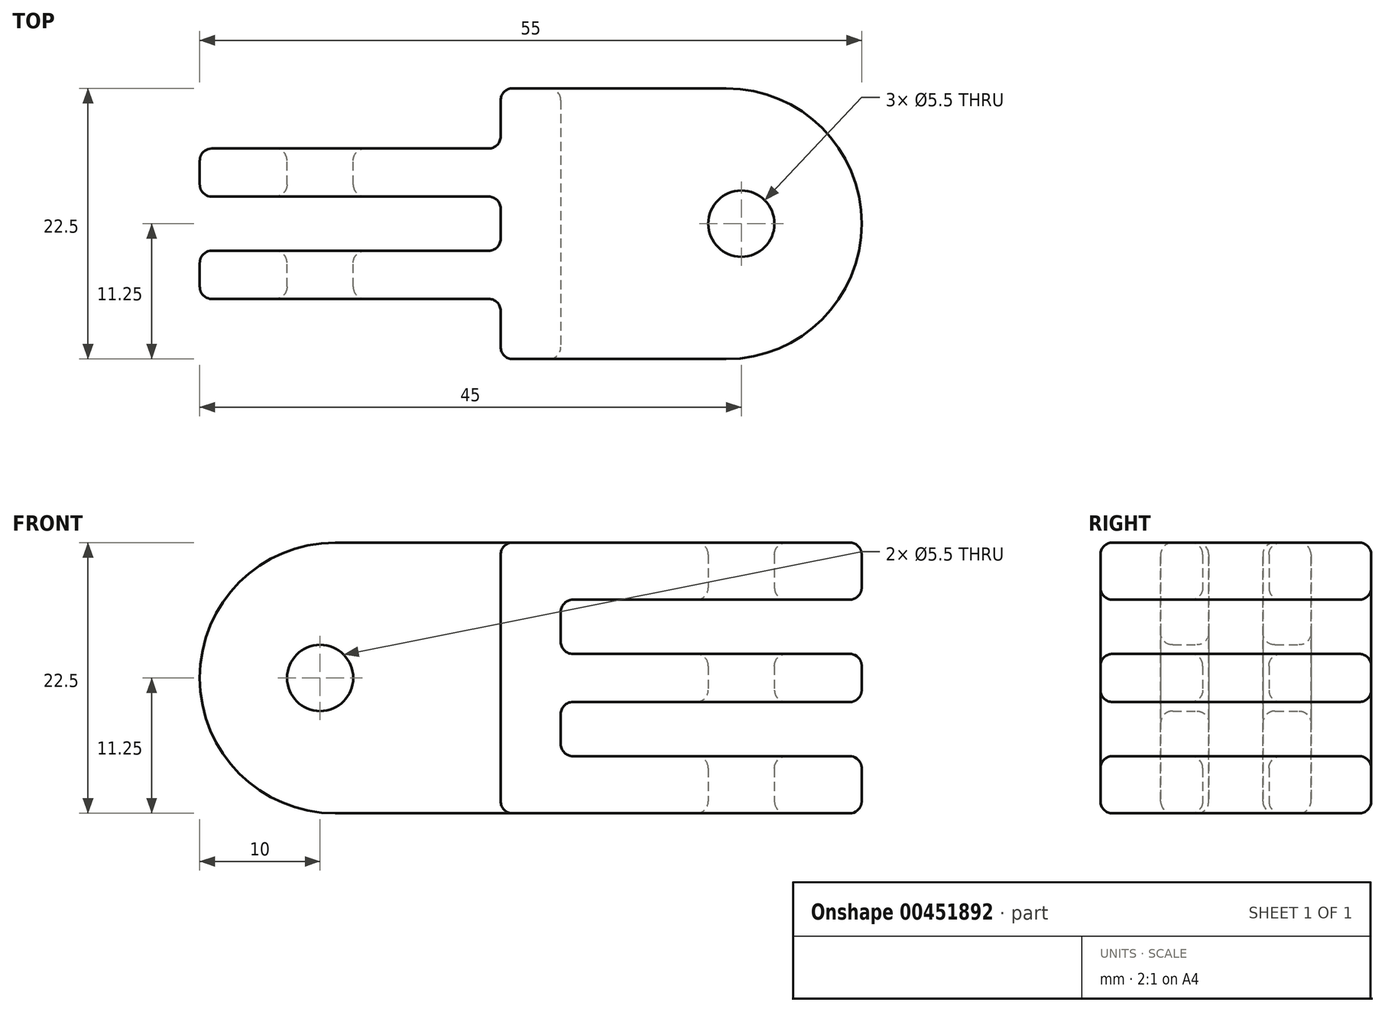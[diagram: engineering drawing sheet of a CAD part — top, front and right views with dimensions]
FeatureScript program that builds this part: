
annotation { "Feature Type Name" : "Feature", "Feature Type Description" : "" }
export const myFeature = defineFeature(function(context is Context, id is Id, definition is map)
    precondition{}
    {
        {
            var Q0;
            Q0=qCreatedBy(makeId("Right.planeOp"),FACE);
            cPlane(context, id + "F0", {"entities" : qUnion([Q0]), "cplaneType" : CPlaneType.OFFSET, "offset" : 55 * mm, "oppositeDirection" : true, "width" : 150 * mm, "height" : 150 * mm});
        }
        {
            var Q0;
            Q0=qCreatedBy(makeId("Front.planeOp"),FACE);
            var sketch = newSketch(context, id + "F1", { "sketchPlane" : qUnion([Q0])});
            skLineSegment(sketch, "E0.bottom", {"start": v(0, -11.25) * mm, "end": v(-43.75, -11.25) * mm});
            skLineSegment(sketch, "E0.top", {"start": v(0, 11.25) * mm, "end": v(-43.75, 11.25) * mm});
            skLineSegment(sketch, "E0.left", {"start": v(0, -11.25) * mm, "end": v(0, 11.25) * mm});
            skPoint(sketch, "E0.middle", {"position": v(-21.87, 0) * mm});
            skArc(sketch, "E1", {"start": v(-43.75, 11.25) * mm, "mid": v(-55, 0) * mm, "end": v(-43.75, -11.25) * mm});
            skCircle(sketch, "E2", {"center": v(-45, 0) * mm, "radius": 2.75 * mm});
            skSolve(sketch);
        }
        {
            var Q0;
            Q0=qSketchRegion(id+"F1",true);
            extrude(context, id + "F2", {"entities" : qUnion([Q0]), "endBound" : BoundingType.SYMMETRIC, "depth" : 22.5 * mm});
        }
        {
            var Q0;
            Q0=qCreatedBy(makeId("Top.planeOp"),FACE);
            var sketch = newSketch(context, id + "F3", { "sketchPlane" : qUnion([Q0])});
            skLineSegment(sketch, "E3.bottom", {"start": v(-55, 2.25) * mm, "end": v(-30, 2.25) * mm});
            skLineSegment(sketch, "E3.top", {"start": v(-55, -2.25) * mm, "end": v(-30, -2.25) * mm});
            skLineSegment(sketch, "E3.left", {"start": v(-55, 2.25) * mm, "end": v(-55, -2.25) * mm});
            skLineSegment(sketch, "E3.right", {"start": v(-30, 2.25) * mm, "end": v(-30, -2.25) * mm});
            skPoint(sketch, "E3.middle", {"position": v(-42.5, 0) * mm});
            skLineSegment(sketch, "E4.bottom", {"start": v(-350.04, 11.25) * mm, "end": v(-30, 11.25) * mm});
            skLineSegment(sketch, "E4.top", {"start": v(-350.04, 6.25) * mm, "end": v(-30, 6.25) * mm});
            skLineSegment(sketch, "E4.left", {"start": v(-350.04, 11.25) * mm, "end": v(-350.04, 6.25) * mm});
            skLineSegment(sketch, "E4.right", {"start": v(-30, 11.25) * mm, "end": v(-30, 6.25) * mm});
            skLineSegment(sketch, "E5.bottom", {"start": v(-55, -11.25) * mm, "end": v(-30, -11.25) * mm});
            skLineSegment(sketch, "E5.top", {"start": v(-55, -6.25) * mm, "end": v(-30, -6.25) * mm});
            skLineSegment(sketch, "E5.left", {"start": v(-55, -11.25) * mm, "end": v(-55, -6.25) * mm});
            skLineSegment(sketch, "E5.right", {"start": v(-30, -11.25) * mm, "end": v(-30, -6.25) * mm});
            skSolve(sketch);
        }
        {
            var Q0;
            Q0=qSketchRegion(id+"F3",true);
            extrude(context, id + "F4", {"entities" : qUnion([Q0]), "operationType" : NewBodyOperationType.REMOVE, "endBound" : BoundingType.SYMMETRIC, "depth" : 50 * mm});
        }
        {
            var Q0;
            Q0=qCreatedBy(makeId("Front.planeOp"),FACE);
            var sketch = newSketch(context, id + "F5", { "sketchPlane" : qUnion([Q0])});
            skLineSegment(sketch, "E6.bottom", {"start": v(-25, 6.5) * mm, "end": v(0, 6.5) * mm});
            skLineSegment(sketch, "E6.top", {"start": v(-25, 2) * mm, "end": v(0, 2) * mm});
            skLineSegment(sketch, "E6.left", {"start": v(-25, 6.5) * mm, "end": v(-25, 2) * mm});
            skLineSegment(sketch, "E6.right", {"start": v(0, 6.5) * mm, "end": v(0, 2) * mm});
            skLineSegment(sketch, "E7.bottom", {"start": v(-25, -6.5) * mm, "end": v(0, -6.5) * mm});
            skLineSegment(sketch, "E7.top", {"start": v(-25, -2) * mm, "end": v(0, -2) * mm});
            skLineSegment(sketch, "E7.left", {"start": v(-25, -6.5) * mm, "end": v(-25, -2) * mm});
            skLineSegment(sketch, "E7.right", {"start": v(0, -6.5) * mm, "end": v(0, -2) * mm});
            skSolve(sketch);
        }
        {
            var Q0;
            Q0 = qSketchRegion(id + "F5", true);
            extrude(context, id + "F6", {"entities" : qUnion([Q0]), "operationType" : NewBodyOperationType.REMOVE, "endBound" : BoundingType.SYMMETRIC, "oppositeDirection" : true, "depth" : 50 * mm});
        }
        {
            var Q0;
            Q0=qCreatedBy(makeId("Top.planeOp"),FACE);
            var sketch = newSketch(context, id + "F7", { "sketchPlane" : qUnion([Q0])});
            skArc(sketch, "E8", {"start": v(-11.25, -11.25) * mm, "mid": v(0, 0) * mm, "end": v(-11.25, 11.25) * mm});
            skLineSegment(sketch, "E9.bottom", {"start": v(-11.25, -11.25) * mm, "end": v(10, -11.25) * mm});
            skLineSegment(sketch, "E9.top", {"start": v(-11.25, 11.25) * mm, "end": v(10, 11.25) * mm});
            skLineSegment(sketch, "E9.right", {"start": v(10, -11.25) * mm, "end": v(10, 11.25) * mm});
            skPoint(sketch, "E9.middle", {"position": v(-0.62, 0) * mm});
            skCircle(sketch, "E10", {"center": v(-10, 0) * mm, "radius": 2.75 * mm});
            skSolve(sketch);
        }
        {
            var Q0;
            Q0 = qSketchRegion(id + "F7", true);
            extrude(context, id + "F8", {"entities" : qUnion([Q0]), "operationType" : NewBodyOperationType.REMOVE, "endBound" : BoundingType.SYMMETRIC, "depth" : 50 * mm});
        }
        {
            var Q0;
            Q0=makeQuery(id+"F2.opExtrude","CAP_FACE",FACE,{"disambiguationData":[OSD([sQuery(id+"F1.wireOp",EDGE,"E0.bottom"),sQuery(id+"F1.wireOp",EDGE,"E0.top"),sQuery(id+"F1.wireOp",EDGE,"E0.left"),sQuery(id+"F1.wireOp",EDGE,"E1"),sQuery(id+"F1.wireOp",EDGE,"E2")])],"isStart":false});
            var Q1;
            Q1=makeQuery(id+"F4.boolean.opBoolean","COPY",FACE,{"derivedFrom":makeQuery(id+"F4.opExtrude","SWEPT_FACE",FACE,{"disambiguationData":[OSD([sQuery(id+"F3.wireOp",EDGE,"E3.top")])]})});
            var Q2;
            Q2=makeQuery(id+"F4.boolean.opBoolean","COPY",FACE,{"derivedFrom":makeQuery(id+"F4.opExtrude","SWEPT_FACE",FACE,{"disambiguationData":[OSD([sQuery(id+"F3.wireOp",EDGE,"E3.bottom")])]})});
            var Q3;
            Q3=makeQuery(id+"F2.opExtrude","CAP_FACE",FACE,{"disambiguationData":[OSD([sQuery(id+"F1.wireOp",EDGE,"E0.bottom"),sQuery(id+"F1.wireOp",EDGE,"E0.top"),sQuery(id+"F1.wireOp",EDGE,"E0.left"),sQuery(id+"F1.wireOp",EDGE,"E1"),sQuery(id+"F1.wireOp",EDGE,"E2")])],"isStart":true});
            var Q4;
            Q4=makeQuery(id+"F4.boolean.opBoolean","COPY",FACE,{"derivedFrom":makeQuery(id+"F4.opExtrude","SWEPT_FACE",FACE,{"disambiguationData":[OSD([sQuery(id+"F3.wireOp",EDGE,"E5.top")])]})});
            var Q5;
            Q5=makeQuery(id+"F4.boolean.opBoolean","COPY",FACE,{"derivedFrom":makeQuery(id+"F4.opExtrude","SWEPT_FACE",FACE,{"disambiguationData":[OSD([sQuery(id+"F3.wireOp",EDGE,"E4.top")])]})});
            var Q6;
            {var subQ2=sQuery(id+"F1.wireOp",EDGE,"E0.left");var subQ3=sQuery(id+"F1.wireOp",EDGE,"E0.top");Q6=makeQuery(id+"F6.boolean.opBoolean","SPLIT",FACE,{"disambiguationData":[TD([makeQuery(id+"F2.opExtrude","SWEPT_FACE",FACE,{"disambiguationData":[OSD([subQ3])]})])],"derivedFrom":makeQuery(id+"F2.opExtrude","SWEPT_FACE",FACE,{"disambiguationData":[OSD([subQ2])]})});}
            var Q7;
            {var subQ2=sQuery(id+"F1.wireOp",EDGE,"E0.left");Q7=makeQuery(id+"F6.boolean.opBoolean","SPLIT",FACE,{"disambiguationData":[TD([makeQuery(id+"F6.opExtrude","SWEPT_FACE",FACE,{"disambiguationData":[OSD([sQuery(id+"F5.wireOp",EDGE,"E6.top")])]})])],"derivedFrom":makeQuery(id+"F2.opExtrude","SWEPT_FACE",FACE,{"disambiguationData":[OSD([subQ2])]})});}
            var Q8;
            {var subQ0=sQuery(id+"F1.wireOp",EDGE,"E0.bottom");var subQ3=sQuery(id+"F1.wireOp",EDGE,"E0.left");Q8=makeQuery(id+"F6.boolean.opBoolean","SPLIT",FACE,{"disambiguationData":[TD([makeQuery(id+"F2.opExtrude","SWEPT_FACE",FACE,{"disambiguationData":[OSD([subQ0])]})])],"derivedFrom":makeQuery(id+"F2.opExtrude","SWEPT_FACE",FACE,{"disambiguationData":[OSD([subQ3])]})});}
            var Q9;
            Q9=makeQuery(id+"F6.boolean.opBoolean","COPY",FACE,{"derivedFrom":makeQuery(id+"F6.opExtrude","SWEPT_FACE",FACE,{"disambiguationData":[OSD([sQuery(id+"F5.wireOp",EDGE,"E6.left")])]})});
            var Q10;
            Q10=makeQuery(id+"F6.boolean.opBoolean","COPY",FACE,{"derivedFrom":makeQuery(id+"F6.opExtrude","SWEPT_FACE",FACE,{"disambiguationData":[OSD([sQuery(id+"F5.wireOp",EDGE,"E7.left")])]})});
            var Q11;
            Q11=makeQuery(id+"F2.opExtrude","SWEPT_FACE",FACE,{"disambiguationData":[OSD([sQuery(id+"F1.wireOp",EDGE,"E0.bottom")])]});
            var Q12;
            Q12=makeQuery(id+"F6.boolean.opBoolean","COPY",FACE,{"derivedFrom":makeQuery(id+"F6.opExtrude","SWEPT_FACE",FACE,{"disambiguationData":[OSD([sQuery(id+"F5.wireOp",EDGE,"E7.bottom")])]})});
            var Q13;
            Q13=makeQuery(id+"F6.boolean.opBoolean","COPY",FACE,{"derivedFrom":makeQuery(id+"F6.opExtrude","SWEPT_FACE",FACE,{"disambiguationData":[OSD([sQuery(id+"F5.wireOp",EDGE,"E6.top")])]})});
            var Q14;
            Q14=makeQuery(id+"F2.opExtrude","SWEPT_FACE",FACE,{"disambiguationData":[OSD([sQuery(id+"F1.wireOp",EDGE,"E0.top")])]});
            var Q15;
            Q15=makeQuery(id+"F6.boolean.opBoolean","COPY",FACE,{"derivedFrom":makeQuery(id+"F6.opExtrude","SWEPT_FACE",FACE,{"disambiguationData":[OSD([sQuery(id+"F5.wireOp",EDGE,"E6.bottom")])]})});
            var Q16;
            Q16=makeQuery(id+"F6.boolean.opBoolean","COPY",FACE,{"derivedFrom":makeQuery(id+"F6.opExtrude","SWEPT_FACE",FACE,{"disambiguationData":[OSD([sQuery(id+"F5.wireOp",EDGE,"E7.top")])]})});
            fillet(context, id + "F9", {"entities" : qUnion([Q0, Q1, Q2, Q3, Q4, Q5, Q6, Q7, Q8, Q9, Q10, Q11, Q12, Q13, Q14, Q15, Q16]), "radius" : 1 * mm, "tangentPropagation" : true, "allowEdgeOverflow" : false});
        }
    });
